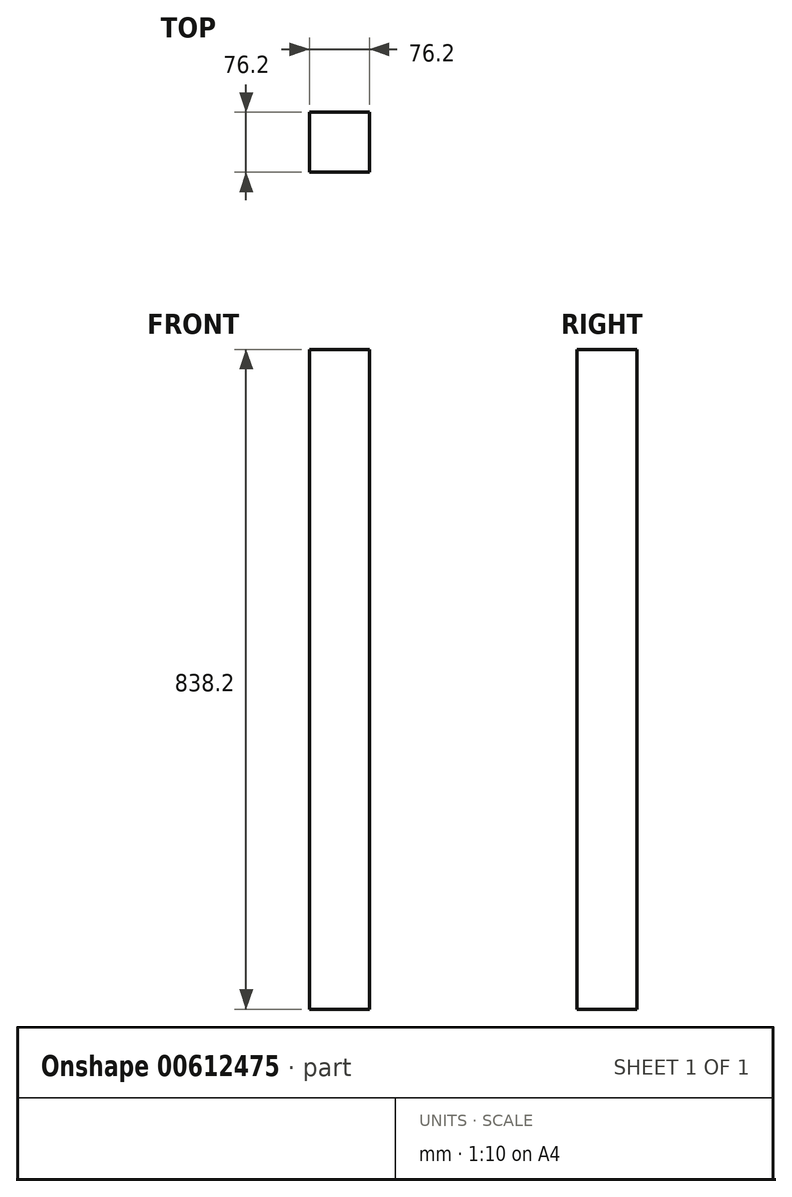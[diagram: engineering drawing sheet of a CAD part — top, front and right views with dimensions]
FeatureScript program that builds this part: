
annotation { "Feature Type Name" : "Feature", "Feature Type Description" : "" }
export const myFeature = defineFeature(function(context is Context, id is Id, definition is map)
    precondition{}
    {
        {
            var Q0;
            Q0=qCreatedBy(makeId("Front.planeOp"),FACE);
            var sketch = newSketch(context, id + "F0", { "sketchPlane" : qUnion([Q0])});
            skLineSegment(sketch, "E0.bottom", {"start": v(0, 298.12) * mm, "end": v(76.2, 298.12) * mm});
            skLineSegment(sketch, "E0.top", {"start": v(0, -540.08) * mm, "end": v(76.2, -540.08) * mm});
            skLineSegment(sketch, "E0.left", {"start": v(0, 298.12) * mm, "end": v(0, -540.08) * mm});
            skLineSegment(sketch, "E0.right", {"start": v(76.2, 298.12) * mm, "end": v(76.2, -540.08) * mm});
            skSolve(sketch);
        }
        {
            var Q0;
            Q0=makeQuery(id+"F0.imprint","IMPRINT",FACE,{"disambiguationData":[TD([[makeQuery(id+"F0.imprint","IMPRINT",EDGE,{"derivedFrom":sQuery(id+"F0.wireOp",EDGE,"E0.bottom")}),-1.0]])]});
            extrude(context, id + "F1", {"entities" : qUnion([Q0]), "depth" : 76.2 * mm, "offsetDistance" : 25.4 * mm});
        }
    });
